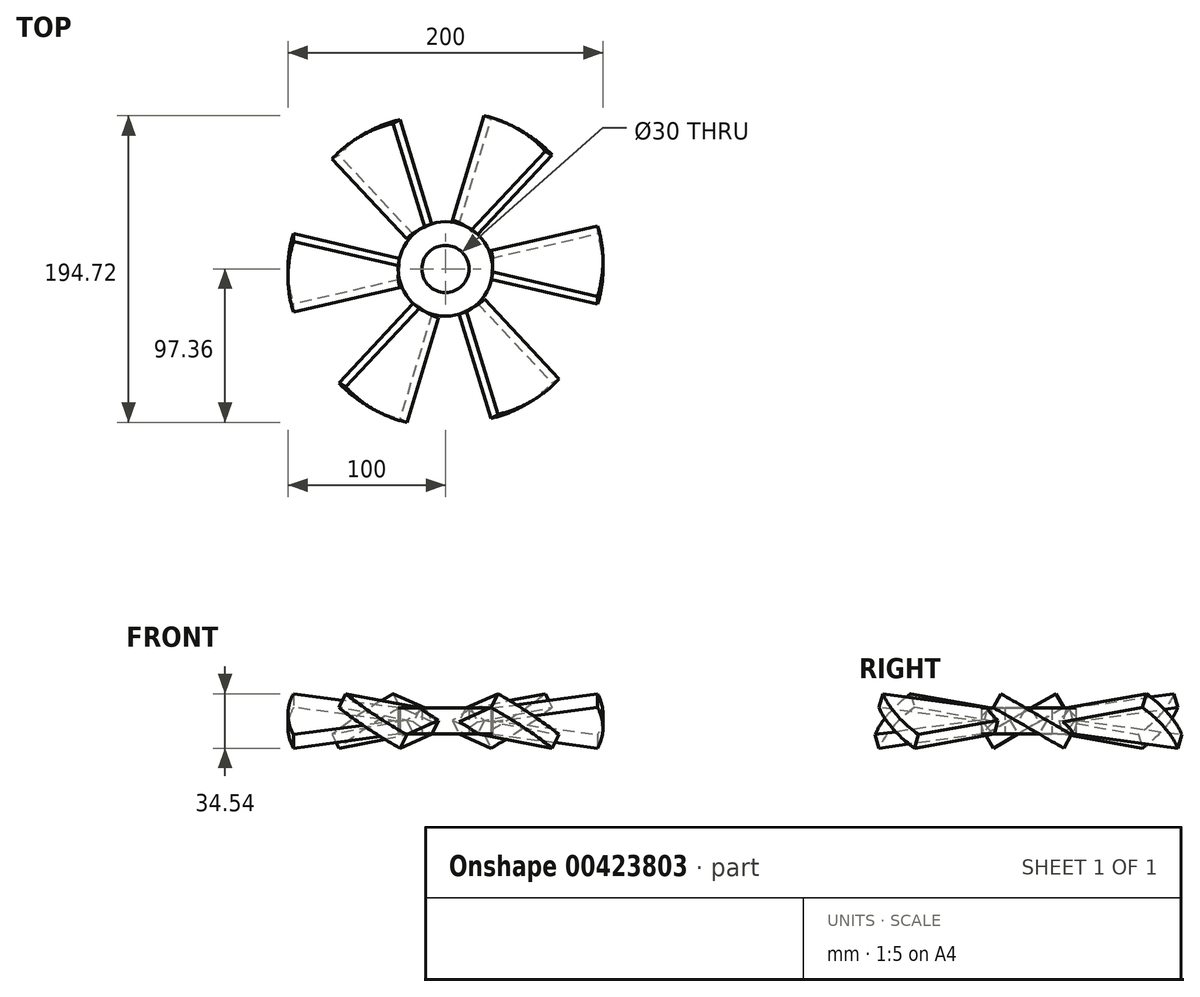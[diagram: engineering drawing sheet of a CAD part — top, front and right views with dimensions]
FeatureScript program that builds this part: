
annotation { "Feature Type Name" : "Feature", "Feature Type Description" : "" }
export const myFeature = defineFeature(function(context is Context, id is Id, definition is map)
    precondition{}
    {
        {
            var Q0;
            Q0=qCreatedBy(makeId("Top.planeOp"),FACE);
            var sketch = newSketch(context, id + "F0", { "sketchPlane" : qUnion([Q0])});
            skCircle(sketch, "E0", {"center": v(0, 0) * mm, "radius": 15 * mm});
            skCircle(sketch, "E1", {"center": v(0, 0) * mm, "radius": 30 * mm});
            skArc(sketch, "E2", {"start": v(96.6, -25.88) * mm, "mid": v(100, 0) * mm, "end": v(96.6, 25.88) * mm});
            skLineSegment(sketch, "E3", {"start": v(28.98, 7.76) * mm, "end": v(96.6, 25.88) * mm});
            skLineSegment(sketch, "E4.MirrorCS", {"start": v(28.98, -7.76) * mm, "end": v(96.6, -25.88) * mm});
            skPoint(sketch, "E5.orphan", {"position": v(101, 27.06) * mm});
            skPoint(sketch, "E6.orphan", {"position": v(101, -27.06) * mm});
            skLineSegment(sketch, "E7", {"start": v(0, 0) * mm, "end": v(-66.12, 0) * mm, "construction": true});
            skSolve(sketch);
        }
        {
            var Q0;
            Q0=makeQuery(id+"F0.imprint","IMPRINT",FACE,{"disambiguationData":[TD([[makeQuery(id+"F0.imprint","IMPRINT",EDGE,{"derivedFrom":sQuery(id+"F0.wireOp",EDGE,"E2")}),1.0]])]});
            extrude(context, id + "F1", {"entities" : qUnion([Q0]), "depth" : 10 * mm});
        }
        {
            var Q0;
            Q0=makeQuery(id+"F1.opExtrude","SWEPT_BODY",BODY,{"disambiguationData":[OSD([sQuery(id+"F0.wireOp",EDGE,"E1"),sQuery(id+"F0.wireOp",EDGE,"E2"),sQuery(id+"F0.wireOp",EDGE,"E3"),sQuery(id+"F0.wireOp",EDGE,"E4.MirrorCS")])]});
            var Q1;
            Q1=sQuery(id+"F0.wireOp",EDGE,"E7");
            transform(context, id + "F2", {"entities" : qUnion([Q0]), "transformType" : TransformType.ROTATION, "transformAxis" : qUnion([Q1]), "angle" : 30 * degree, "makeCopy" : false});
        }
        {
            var Q0;
            Q0=qCreatedBy(makeId("Right.planeOp"),FACE);
            var sketch = newSketch(context, id + "F3", { "sketchPlane" : qUnion([Q0])});
            skLineSegment(sketch, "E8", {"start": v(0, 0) * mm, "end": v(0, 43.1) * mm, "construction": true});
            skSolve(sketch);
        }
        {
            var Q0;
            Q0=makeQuery(id+"F1.opExtrude","SWEPT_BODY",BODY,{"disambiguationData":[OSD([sQuery(id+"F0.wireOp",EDGE,"E1"),sQuery(id+"F0.wireOp",EDGE,"E2"),sQuery(id+"F0.wireOp",EDGE,"E3"),sQuery(id+"F0.wireOp",EDGE,"E4.MirrorCS")])]});
            var Q1;
            Q1=sQuery(id+"F3.wireOp",EDGE,"E8");
            circularPattern(context, id + "F4", {"entities" : qUnion([Q0]), "axis" : qUnion([Q1]), "angle" : 360 * degree, "instanceCount" : 6, "equalSpace" : true});
        }
        {
            var Q0;
            Q0=makeQuery(id+"F0.imprint","IMPRINT",FACE,{"disambiguationData":[TD([[makeQuery(id+"F0.imprint","IMPRINT",EDGE,{"derivedFrom":sQuery(id+"F0.wireOp",EDGE,"E0")}),-1.0]])]});
            var Q1;
            Q1=makeQuery(id+"F4.opPattern","COPY",VERTEX,{"derivedFrom":makeQuery(id+"F1.opExtrude","CAP_VERTEX",VERTEX,{"disambiguationData":[OSD([sQuery(id+"F0.wireOp",EDGE,"E1"),sQuery(id+"F0.wireOp",EDGE,"E4.MirrorCS")])],"isStart":false}),"instanceName":"2"});
            var Q2;
            Q2=makeQuery(id+"F4.opPattern","COPY",VERTEX,{"derivedFrom":makeQuery(id+"F1.opExtrude","CAP_VERTEX",VERTEX,{"disambiguationData":[OSD([sQuery(id+"F0.wireOp",EDGE,"E1"),sQuery(id+"F0.wireOp",EDGE,"E3")])],"isStart":true}),"instanceName":"5"});
            extrude(context, id + "F5", {"entities" : qUnion([Q0]), "endBound" : BoundingType.UP_TO_VERTEX, "endBoundEntityVertex" : qUnion([Q1]), "depth" : 25 * mm, "hasSecondDirection" : true, "secondDirectionBound" : SecondDirectionBoundingType.UP_TO_VERTEX, "secondDirectionOppositeDirection" : true, "secondDirectionBoundEntityVertex" : qUnion([Q2]), "secondDirectionDepth" : 25 * mm});
        }
    });
